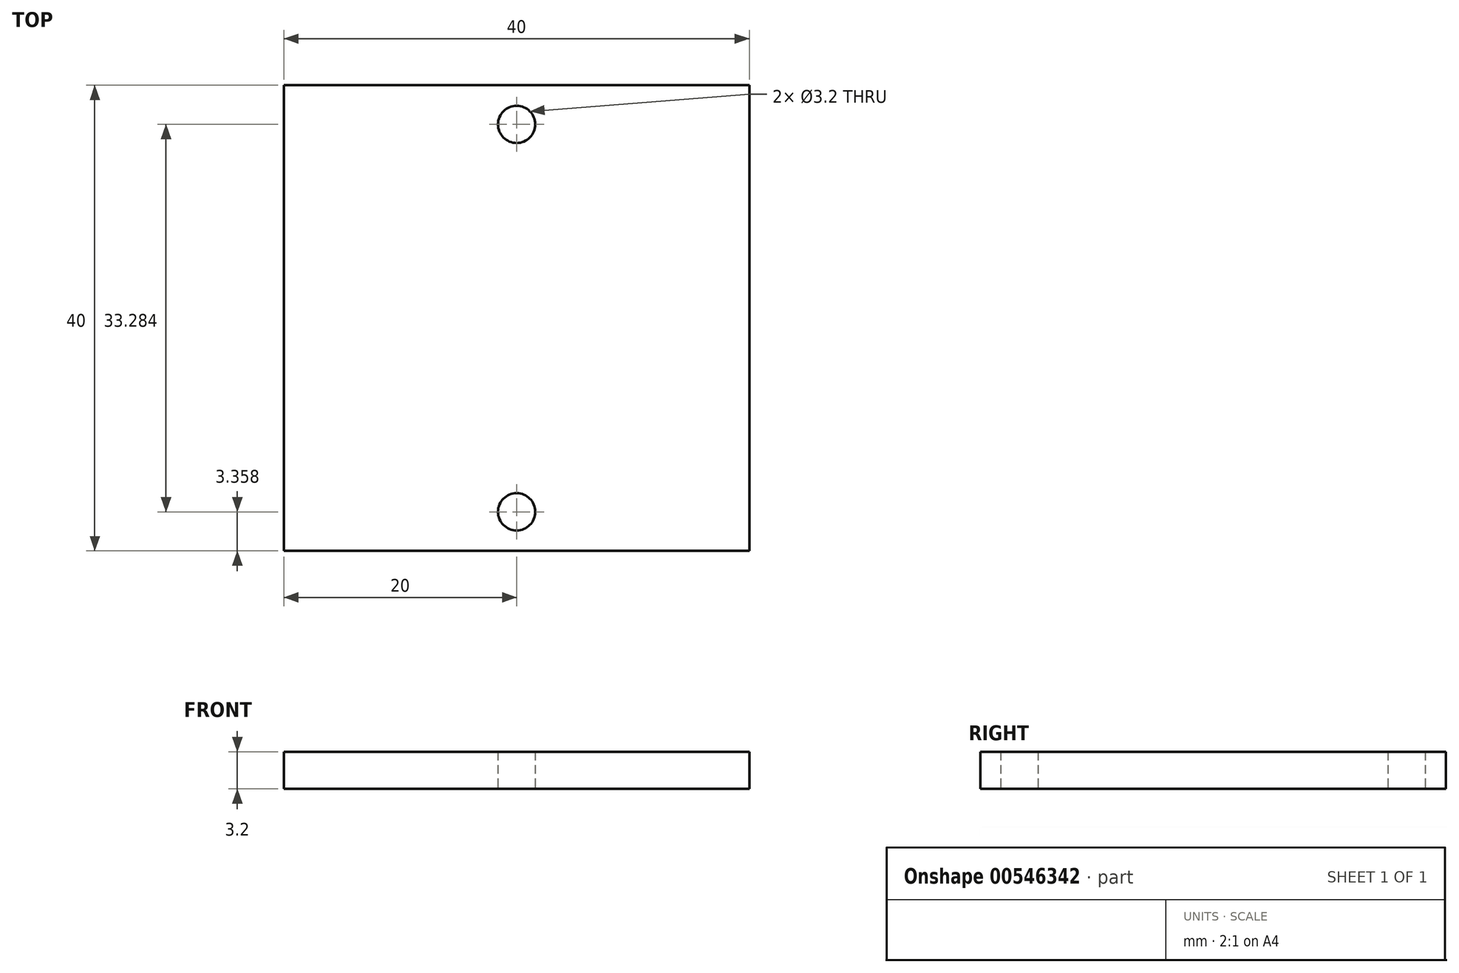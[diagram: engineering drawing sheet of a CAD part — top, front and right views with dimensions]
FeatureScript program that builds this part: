
annotation { "Feature Type Name" : "Feature", "Feature Type Description" : "" }
export const myFeature = defineFeature(function(context is Context, id is Id, definition is map)
    precondition{}
    {
        {
            var Q0;
            Q0=qCreatedBy(makeId("Top.planeOp"),FACE);
            var sketch = newSketch(context, id + "F0", { "sketchPlane" : qUnion([Q0])});
            skLineSegment(sketch, "E0.bottom", {"start": v(20, 20) * mm, "end": v(-20, 20) * mm});
            skLineSegment(sketch, "E0.top", {"start": v(20, -20) * mm, "end": v(-20, -20) * mm});
            skLineSegment(sketch, "E0.left", {"start": v(20, 20) * mm, "end": v(20, -20) * mm});
            skLineSegment(sketch, "E0.right", {"start": v(-20, 20) * mm, "end": v(-20, -20) * mm});
            skPoint(sketch, "E0.middle", {"position": v(0, 0) * mm});
            skLineSegment(sketch, "E1", {"start": v(0, 16.64) * mm, "end": v(0, -16.64) * mm, "construction": true});
            skCircle(sketch, "E2", {"center": v(0, 16.64) * mm, "radius": 1.6 * mm});
            skCircle(sketch, "E3", {"center": v(0, -16.64) * mm, "radius": 1.6 * mm});
            skSolve(sketch);
        }
        {
            var Q0;
            Q0 = qSketchRegion(id + "F0", true);
            extrude(context, id + "F1", {"entities" : qUnion([Q0]), "depth" : 3.2 * mm, "offsetDistance" : 25 * mm});
        }
    });
